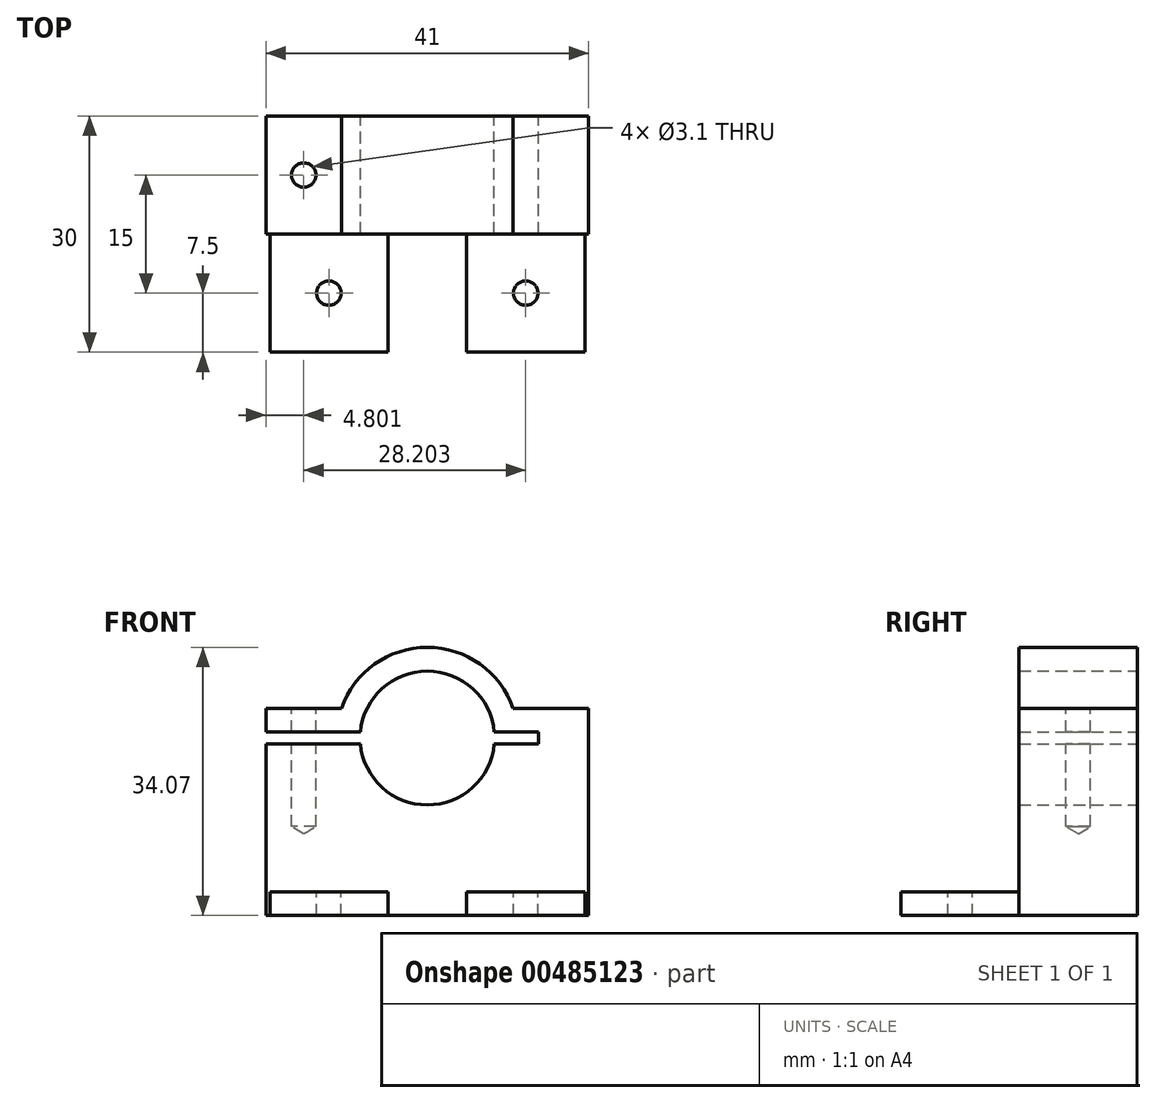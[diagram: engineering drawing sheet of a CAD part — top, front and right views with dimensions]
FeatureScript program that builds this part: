
annotation { "Feature Type Name" : "Feature", "Feature Type Description" : "" }
export const myFeature = defineFeature(function(context is Context, id is Id, definition is map)
    precondition{}
    {
        {
            var Q0;
            Q0=qCreatedBy(makeId("Front.planeOp"),FACE);
            var sketch = newSketch(context, id + "F0", { "sketchPlane" : qUnion([Q0])});
            skLineSegment(sketch, "E0.bottom", {"start": v(-19.42, 11.05) * mm, "end": v(-7.42, 11.05) * mm, "construction": true});
            skLineSegment(sketch, "E0.left", {"start": v(-19.42, 11.05) * mm, "end": v(-19.42, 8.05) * mm, "construction": true});
            skLineSegment(sketch, "E0.right", {"start": v(-7.42, 11.05) * mm, "end": v(-7.42, 8.05) * mm, "construction": true});
            skLineSegment(sketch, "E1.top", {"start": v(9.58, 11.05) * mm, "end": v(23.18, 11.05) * mm, "construction": true});
            skLineSegment(sketch, "E1.left", {"start": v(9.58, 8.05) * mm, "end": v(9.58, 11.05) * mm, "construction": true});
            skLineSegment(sketch, "E2", {"start": v(-10.42, 11.05) * mm, "end": v(-10.42, 8.05) * mm, "construction": true});
            skLineSegment(sketch, "E3", {"start": v(12.58, 11.05) * mm, "end": v(12.58, 8.05) * mm, "construction": true});
            skLineSegment(sketch, "E4", {"start": v(-19.42, 11.05) * mm, "end": v(-7.42, 11.05) * mm});
            skLineSegment(sketch, "E5", {"start": v(9.58, 11.05) * mm, "end": v(12.58, 11.05) * mm});
            skLineSegment(sketch, "E6", {"start": v(9.58, 11.05) * mm, "end": v(9.58, 8.05) * mm});
            skLineSegment(sketch, "E7", {"start": v(-7.42, 11.05) * mm, "end": v(-7.42, 8.05) * mm});
            skLineSegment(sketch, "E8", {"start": v(-19.42, 11.05) * mm, "end": v(-19.42, 8.05) * mm});
            skLineSegment(sketch, "E9", {"start": v(21.58, 8.05) * mm, "end": v(12.58, 8.05) * mm, "construction": true});
            skLineSegment(sketch, "E10.bottom", {"start": v(23.18, 12.55) * mm, "end": v(9.58, 12.55) * mm, "construction": true});
            skLineSegment(sketch, "E10.top", {"start": v(21.58, 15.55) * mm, "end": v(9.58, 15.55) * mm, "construction": true});
            skLineSegment(sketch, "E10.right", {"start": v(9.58, 12.55) * mm, "end": v(9.58, 15.55) * mm, "construction": true});
            skLineSegment(sketch, "E11", {"start": v(12.58, 11.05) * mm, "end": v(12.58, 15.55) * mm, "construction": true});
            skLineSegment(sketch, "E12.bottom", {"start": v(-7.42, 12.55) * mm, "end": v(-19.42, 12.55) * mm, "construction": true});
            skLineSegment(sketch, "E12.top", {"start": v(-7.42, 15.55) * mm, "end": v(-19.42, 15.55) * mm, "construction": true});
            skLineSegment(sketch, "E12.left", {"start": v(-7.42, 12.55) * mm, "end": v(-7.42, 15.55) * mm, "construction": true});
            skLineSegment(sketch, "E12.right", {"start": v(-19.42, 12.55) * mm, "end": v(-19.42, 15.55) * mm, "construction": true});
            skLineSegment(sketch, "E13", {"start": v(9.58, 12.55) * mm, "end": v(9.58, 11.05) * mm, "construction": true});
            skPoint(sketch, "E14", {"position": v(9.58, 11.8) * mm});
            skLineSegment(sketch, "E15", {"start": v(-7.42, 12.55) * mm, "end": v(-7.42, 11.05) * mm, "construction": true});
            skLineSegment(sketch, "E16", {"start": v(-7.42, 11.8) * mm, "end": v(9.58, 11.8) * mm, "construction": true});
            skPoint(sketch, "E17", {"position": v(1.08, 11.8) * mm});
            skArc(sketch, "E18", {"start": v(9.58, 12.55) * mm, "mid": v(1.08, 20.32) * mm, "end": v(-7.42, 12.55) * mm, "construction": true});
            skArc(sketch, "E19", {"start": v(-7.42, 11.05) * mm, "mid": v(1.08, 3.25) * mm, "end": v(9.58, 11.05) * mm, "construction": true});
            skArc(sketch, "E20", {"start": v(12.58, 12.55) * mm, "mid": v(1.08, 23.35) * mm, "end": v(-10.42, 12.55) * mm, "construction": true});
            skLineSegment(sketch, "E21", {"start": v(15.18, 12.55) * mm, "end": v(15.18, 11.05) * mm, "construction": true});
            skLineSegment(sketch, "E22", {"start": v(-19.42, 8.05) * mm, "end": v(-9.8, 8.05) * mm, "construction": true});
            skLineSegment(sketch, "E23", {"start": v(-19.42, 12.55) * mm, "end": v(-7.42, 12.55) * mm});
            skLineSegment(sketch, "E24", {"start": v(-19.42, 12.55) * mm, "end": v(-19.42, 15.55) * mm});
            skLineSegment(sketch, "E25", {"start": v(-19.42, 15.55) * mm, "end": v(-9.82, 15.55) * mm});
            skLineSegment(sketch, "E26", {"start": v(9.58, 11.05) * mm, "end": v(15.18, 11.05) * mm});
            skLineSegment(sketch, "E27", {"start": v(15.18, 11.05) * mm, "end": v(15.18, 12.55) * mm});
            skLineSegment(sketch, "E28", {"start": v(15.18, 12.55) * mm, "end": v(9.58, 12.55) * mm});
            skLineSegment(sketch, "E29", {"start": v(21.58, 15.55) * mm, "end": v(11.99, 15.55) * mm});
            skArc(sketch, "E30", {"start": v(9.58, 12.55) * mm, "mid": v(1.08, 20.3) * mm, "end": v(-7.42, 12.55) * mm});
            skArc(sketch, "E31", {"start": v(-7.42, 11.05) * mm, "mid": v(1.08, 3.3) * mm, "end": v(9.58, 11.05) * mm});
            skArc(sketch, "E32", {"start": v(-9.8, 8.05) * mm, "mid": v(1.08, 0.4) * mm, "end": v(11.96, 8.05) * mm, "construction": true});
            skArc(sketch, "E33", {"start": v(11.99, 15.55) * mm, "mid": v(1.08, 23.32) * mm, "end": v(-9.82, 15.55) * mm});
            skLineSegment(sketch, "E34", {"start": v(21.58, 15.55) * mm, "end": v(21.58, 8.05) * mm});
            skLineSegment(sketch, "E35", {"start": v(12.58, 8.05) * mm, "end": v(11.96, 8.05) * mm});
            skLineSegment(sketch, "E36.bottom", {"start": v(-19.42, 8.05) * mm, "end": v(21.58, 8.05) * mm, "construction": true});
            skLineSegment(sketch, "E36.top", {"start": v(-19.42, -10.75) * mm, "end": v(21.58, -10.75) * mm, "construction": true});
            skLineSegment(sketch, "E36.left", {"start": v(-19.42, 8.05) * mm, "end": v(-19.42, -10.75) * mm, "construction": true});
            skLineSegment(sketch, "E36.right", {"start": v(21.58, 8.05) * mm, "end": v(21.58, -10.75) * mm, "construction": true});
            skLineSegment(sketch, "E37", {"start": v(-19.42, 8.05) * mm, "end": v(-19.42, -10.75) * mm});
            skLineSegment(sketch, "E38", {"start": v(-19.42, -10.75) * mm, "end": v(21.58, -10.75) * mm});
            skLineSegment(sketch, "E39", {"start": v(21.58, -10.75) * mm, "end": v(21.58, 8.05) * mm});
            skSolve(sketch);
        }
        {
            var Q0;
            Q0=makeQuery(id+"F0.imprint","IMPRINT",FACE,{"disambiguationData":[TD([[makeQuery(id+"F0.imprint","IMPRINT",EDGE,{"derivedFrom":sQuery(id+"F0.wireOp",EDGE,"E4")}),-1.0]])]});
            extrude(context, id + "F1", {"entities" : qUnion([Q0]), "depth" : 15 * mm, "offsetDistance" : 25 * mm});
        }
        {
            var Q0;
            Q0=makeQuery(id+"F1.opExtrude","SWEPT_FACE",FACE,{"disambiguationData":[OSD([sQuery(id+"F0.wireOp",EDGE,"E25")])]});
            var sketch = newSketch(context, id + "F2", { "sketchPlane" : qUnion([Q0])});
            skLineSegment(sketch, "E40", {"start": v(-14.62, 0) * mm, "end": v(-14.62, -15) * mm, "construction": true});
            skCircle(sketch, "E41", {"center": v(-14.62, -7.5) * mm, "radius": 1.5 * mm, "construction": true});
            skSolve(sketch);
        }
        {
            var Q0;
            Q0=sQuery(id+"F2.wireOp",VERTEX,"E41.center");
            var Q1;
            Q1=makeQuery(id+"F1.opExtrude","SWEPT_BODY",BODY,{"disambiguationData":[OSD([sQuery(id+"F0.wireOp",EDGE,"E4"),sQuery(id+"F0.wireOp",EDGE,"E8"),sQuery(id+"F0.wireOp",EDGE,"E23"),sQuery(id+"F0.wireOp",EDGE,"E24"),sQuery(id+"F0.wireOp",EDGE,"E25"),sQuery(id+"F0.wireOp",EDGE,"E26"),sQuery(id+"F0.wireOp",EDGE,"E27"),sQuery(id+"F0.wireOp",EDGE,"E28"),sQuery(id+"F0.wireOp",EDGE,"E29"),sQuery(id+"F0.wireOp",EDGE,"E30"),sQuery(id+"F0.wireOp",EDGE,"E31"),sQuery(id+"F0.wireOp",EDGE,"E33"),sQuery(id+"F0.wireOp",EDGE,"E34"),sQuery(id+"F0.wireOp",EDGE,"E37"),sQuery(id+"F0.wireOp",EDGE,"E38"),sQuery(id+"F0.wireOp",EDGE,"E39")])]});
            hole(context, id + "F3", {"style" : HoleStyle.SIMPLE, "endStyle" : HoleEndStyle.BLIND, "holeDiameter" : 3.1 * mm, "holeDepth" : 15 * mm, "isTappedThrough" : true, "tappedDepth" : 12 * mm, "tapClearance" : 3, "locations" : qUnion([Q0]), "scope" : qUnion([Q1])});
        }
        {
            var Q0;
            Q0=makeQuery(id+"F1.opExtrude","CAP_FACE",FACE,{"disambiguationData":[OSD([sQuery(id+"F0.wireOp",EDGE,"E4"),sQuery(id+"F0.wireOp",EDGE,"E8"),sQuery(id+"F0.wireOp",EDGE,"E23"),sQuery(id+"F0.wireOp",EDGE,"E24"),sQuery(id+"F0.wireOp",EDGE,"E25"),sQuery(id+"F0.wireOp",EDGE,"E26"),sQuery(id+"F0.wireOp",EDGE,"E27"),sQuery(id+"F0.wireOp",EDGE,"E28"),sQuery(id+"F0.wireOp",EDGE,"E29"),sQuery(id+"F0.wireOp",EDGE,"E30"),sQuery(id+"F0.wireOp",EDGE,"E31"),sQuery(id+"F0.wireOp",EDGE,"E33"),sQuery(id+"F0.wireOp",EDGE,"E34"),sQuery(id+"F0.wireOp",EDGE,"E37"),sQuery(id+"F0.wireOp",EDGE,"E38"),sQuery(id+"F0.wireOp",EDGE,"E39")])],"isStart":false});
            var sketch = newSketch(context, id + "F4", { "sketchPlane" : qUnion([Q0])});
            skLineSegment(sketch, "E42.bottom", {"start": v(-19.42, 1.93) * mm, "end": v(21.58, 1.93) * mm, "construction": true});
            skLineSegment(sketch, "E42.top", {"start": v(-19.42, -10.75) * mm, "end": v(21.58, -10.75) * mm, "construction": true});
            skLineSegment(sketch, "E42.left", {"start": v(-19.42, 1.93) * mm, "end": v(-19.42, -10.75) * mm, "construction": true});
            skLineSegment(sketch, "E42.right", {"start": v(21.58, 1.93) * mm, "end": v(21.58, -10.75) * mm, "construction": true});
            skLineSegment(sketch, "E43", {"start": v(1.08, 3.3) * mm, "end": v(1.08, -10.75) * mm, "construction": true});
            skLineSegment(sketch, "E44", {"start": v(-11.42, -10.75) * mm, "end": v(-11.42, 1.93) * mm, "construction": true});
            skLineSegment(sketch, "E45", {"start": v(13.58, -10.75) * mm, "end": v(13.58, 1.93) * mm, "construction": true});
            skLineSegment(sketch, "E46.bottom", {"start": v(-18.92, -10.75) * mm, "end": v(-3.92, -10.75) * mm});
            skLineSegment(sketch, "E46.top", {"start": v(-18.92, -7.75) * mm, "end": v(-3.92, -7.75) * mm});
            skLineSegment(sketch, "E46.left", {"start": v(-18.92, -10.75) * mm, "end": v(-18.92, -7.75) * mm});
            skLineSegment(sketch, "E46.right", {"start": v(-3.92, -10.75) * mm, "end": v(-3.92, -7.75) * mm});
            skLineSegment(sketch, "E47.bottom", {"start": v(6.08, -10.75) * mm, "end": v(21.08, -10.75) * mm});
            skLineSegment(sketch, "E47.top", {"start": v(6.08, -7.75) * mm, "end": v(21.08, -7.75) * mm});
            skLineSegment(sketch, "E47.left", {"start": v(6.08, -10.75) * mm, "end": v(6.08, -7.75) * mm});
            skLineSegment(sketch, "E47.right", {"start": v(21.08, -10.75) * mm, "end": v(21.08, -7.75) * mm});
            skSolve(sketch);
        }
        {
            var Q0;
            Q0=makeQuery(id+"F4.imprint","IMPRINT",FACE,{"disambiguationData":[TD([[makeQuery(id+"F4.imprint","IMPRINT",EDGE,{"derivedFrom":sQuery(id+"F4.wireOp",EDGE,"E47.bottom")}),1.0]])]});
            var Q1;
            Q1=makeQuery(id+"F4.imprint","IMPRINT",FACE,{"disambiguationData":[TD([[makeQuery(id+"F4.imprint","IMPRINT",EDGE,{"derivedFrom":sQuery(id+"F4.wireOp",EDGE,"E46.bottom")}),1.0]])]});
            extrude(context, id + "F5", {"entities" : qUnion([Q0, Q1]), "operationType" : NewBodyOperationType.ADD, "depth" : 15 * mm, "offsetDistance" : 25 * mm});
        }
        {
            var Q0;
            Q0=makeQuery(id+"F5.opExtrude","SWEPT_FACE",FACE,{"disambiguationData":[OSD([sQuery(id+"F4.wireOp",EDGE,"E46.top")])]});
            var sketch = newSketch(context, id + "F6", { "sketchPlane" : qUnion([Q0])});
            skLineSegment(sketch, "E48", {"start": v(-11.42, -15) * mm, "end": v(-11.42, -30) * mm, "construction": true});
            skCircle(sketch, "E49", {"center": v(-11.42, -22.5) * mm, "radius": 1.5 * mm, "construction": true});
            skSolve(sketch);
        }
        {
            var Q0;
            Q0=makeQuery(id+"F5.opExtrude","SWEPT_FACE",FACE,{"disambiguationData":[OSD([sQuery(id+"F4.wireOp",EDGE,"E47.top")])]});
            var sketch = newSketch(context, id + "F7", { "sketchPlane" : qUnion([Q0])});
            skLineSegment(sketch, "E50", {"start": v(13.58, -15) * mm, "end": v(13.58, -30) * mm, "construction": true});
            skCircle(sketch, "E51", {"center": v(13.58, -22.5) * mm, "radius": 1.5 * mm, "construction": true});
            skSolve(sketch);
        }
        {
            var Q0;
            Q0=sQuery(id+"F6.wireOp",VERTEX,"E49.center");
            var Q1;
            Q1=sQuery(id+"F7.wireOp",VERTEX,"E51.center");
            var Q2;
            Q2=makeQuery(id+"F1.opExtrude","SWEPT_BODY",BODY,{"disambiguationData":[OSD([sQuery(id+"F0.wireOp",EDGE,"E4"),sQuery(id+"F0.wireOp",EDGE,"E8"),sQuery(id+"F0.wireOp",EDGE,"E23"),sQuery(id+"F0.wireOp",EDGE,"E24"),sQuery(id+"F0.wireOp",EDGE,"E25"),sQuery(id+"F0.wireOp",EDGE,"E26"),sQuery(id+"F0.wireOp",EDGE,"E27"),sQuery(id+"F0.wireOp",EDGE,"E28"),sQuery(id+"F0.wireOp",EDGE,"E29"),sQuery(id+"F0.wireOp",EDGE,"E30"),sQuery(id+"F0.wireOp",EDGE,"E31"),sQuery(id+"F0.wireOp",EDGE,"E33"),sQuery(id+"F0.wireOp",EDGE,"E34"),sQuery(id+"F0.wireOp",EDGE,"E37"),sQuery(id+"F0.wireOp",EDGE,"E38"),sQuery(id+"F0.wireOp",EDGE,"E39")])]});
            hole(context, id + "F8", {"style" : HoleStyle.SIMPLE, "endStyle" : HoleEndStyle.BLIND, "holeDiameter" : 3.1 * mm, "holeDepth" : 3 * mm, "isTappedThrough" : true, "tappedDepth" : 12 * mm, "tapClearance" : 3, "locations" : qUnion([Q0, Q1]), "scope" : qUnion([Q2])});
        }
    });
